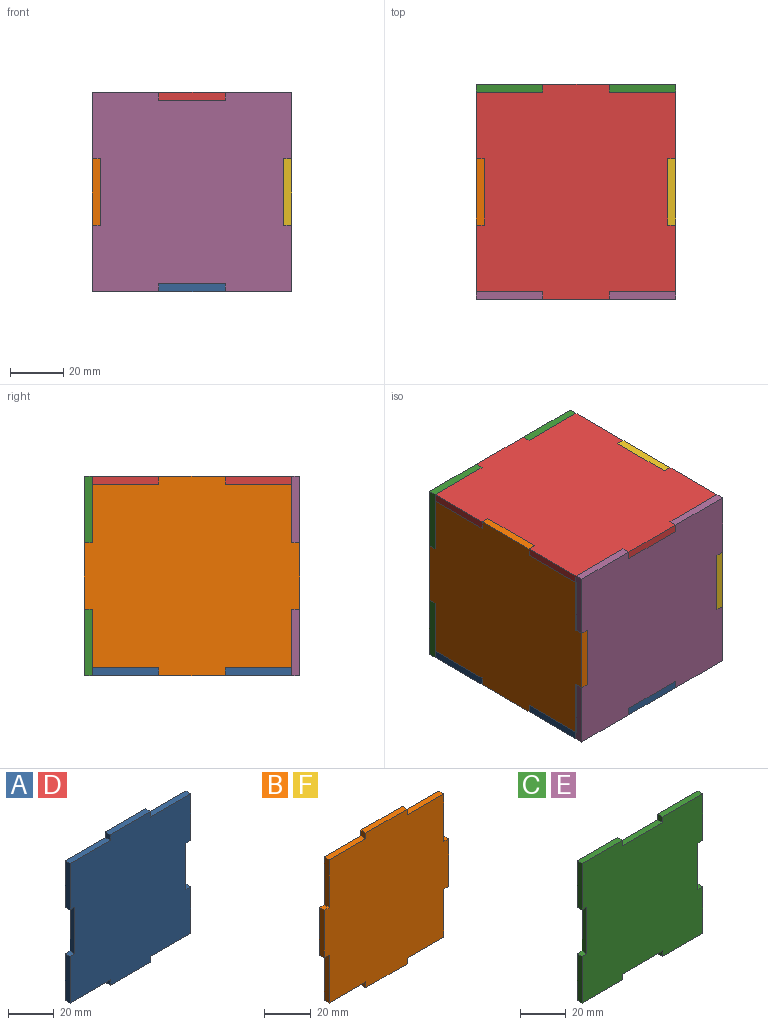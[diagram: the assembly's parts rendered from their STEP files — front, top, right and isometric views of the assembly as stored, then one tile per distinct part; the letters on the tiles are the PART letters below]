
ASSEMBLY  parts=6 mates=2
PART A: 22 faces, bbox 75x3x81 mm
  f0: plane 25x3mm, normal (0,0,1), area 75mm2, adj f1,f19,f20,f21
  f1: plane 3x3mm, normal (1,0,0), area 9mm2, adj f0,f2,f20,f21
  f2: plane 25x3mm, normal (0,0,1), area 75mm2, adj f1,f3,f20,f21
  f3: plane 3x3mm, normal (-1,0,0), area 9mm2, adj f2,f4,f20,f21
  f4: plane 25x3mm, normal (0,0,1), area 75mm2, adj f3,f5,f20,f21
  f5: plane 25x3mm, normal (-1,0,0), area 75mm2, adj f4,f6,f20,f21
  f6: plane 3x3mm, normal (0,0,-1), area 9mm2, adj f5,f7,f20,f21
  f7: plane 25x3mm, normal (-1,0,0), area 75mm2, adj f6,f8,f20,f21
  f8: plane 3x3mm, normal (0,0,1), area 9mm2, adj f7,f9,f20,f21
  f9: plane 25x3mm, normal (-1,0,0), area 75mm2, adj f8,f10,f20,f21
  f10: plane 25x3mm, normal (0,0,-1), area 75mm2, adj f9,f11,f20,f21
  f11: plane 3x3mm, normal (-1,0,0), area 9mm2, adj f10,f12,f20,f21
  f12: plane 25x3mm, normal (0,0,-1), area 75mm2, adj f11,f13,f20,f21
  f13: plane 3x3mm, normal (1,0,0), area 9mm2, adj f12,f14,f20,f21
  f14: plane 25x3mm, normal (0,0,-1), area 75mm2, adj f13,f15,f20,f21
  f15: plane 25x3mm, normal (1,0,0), area 75mm2, adj f14,f16,f20,f21
  f16: plane 3x3mm, normal (0,0,1), area 9mm2, adj f15,f17,f20,f21
  f17: plane 25x3mm, normal (1,0,0), area 75mm2, adj f16,f18,f20,f21
  f18: plane 3x3mm, normal (0,0,-1), area 9mm2, adj f17,f19,f20,f21
  f19: plane 25x3mm, normal (1,0,0), area 75mm2, adj f0,f18,f20,f21
  f20: plane 81x75mm, normal (0,-1,0), area 5625mm2, adj f0,f1,f2,f3,f4,f5,f6,f7
  f21: plane 81x75mm, normal (0,1,0), area 5625mm2, adj f0,f1,f2,f3,f4,f5,f6,f7
PART B: 22 faces, bbox 75x3x81 mm
  f0: plane 25x3mm, normal (0,0,1), area 75mm2, adj f1,f19,f20,f21
  f1: plane 3x3mm, normal (-1,0,0), area 9mm2, adj f0,f2,f20,f21
  f2: plane 22x3mm, normal (0,0,1), area 66mm2, adj f1,f3,f20,f21
  f3: plane 25x3mm, normal (-1,0,0), area 75mm2, adj f2,f4,f20,f21
  f4: plane 3x3mm, normal (0,0,1), area 9mm2, adj f3,f5,f20,f21
  f5: plane 25x3mm, normal (-1,0,0), area 75mm2, adj f4,f6,f20,f21
  f6: plane 3x3mm, normal (0,0,-1), area 9mm2, adj f5,f7,f20,f21
  f7: plane 25x3mm, normal (-1,0,0), area 75mm2, adj f6,f8,f20,f21
  f8: plane 22x3mm, normal (0,0,-1), area 66mm2, adj f7,f9,f20,f21
  f9: plane 3x3mm, normal (-1,0,0), area 9mm2, adj f8,f10,f20,f21
  f10: plane 25x3mm, normal (0,0,-1), area 75mm2, adj f9,f11,f20,f21
  f11: plane 3x3mm, normal (1,0,0), area 9mm2, adj f10,f12,f20,f21
  f12: plane 22x3mm, normal (0,0,-1), area 66mm2, adj f11,f13,f20,f21
  f13: plane 25x3mm, normal (1,0,0), area 75mm2, adj f12,f14,f20,f21
  f14: plane 3x3mm, normal (0,0,-1), area 9mm2, adj f13,f15,f20,f21
  f15: plane 25x3mm, normal (1,0,0), area 75mm2, adj f14,f16,f20,f21
  f16: plane 3x3mm, normal (0,0,1), area 9mm2, adj f15,f17,f20,f21
  f17: plane 25x3mm, normal (1,0,0), area 75mm2, adj f16,f18,f20,f21
  f18: plane 22x3mm, normal (0,0,1), area 66mm2, adj f17,f19,f20,f21
  f19: plane 3x3mm, normal (1,0,0), area 9mm2, adj f0,f18,f20,f21
  f20: plane 81x75mm, normal (0,-1,0), area 5475mm2, adj f0,f1,f2,f3,f4,f5,f6,f7
  f21: plane 81x75mm, normal (0,1,0), area 5475mm2, adj f0,f1,f2,f3,f4,f5,f6,f7
PART C: 22 faces, bbox 75x3x75 mm
  f0: plane 3x3mm, normal (1,0,0), area 9mm2, adj f1,f19,f20,f21
  f1: plane 25x3mm, normal (0,0,1), area 75mm2, adj f0,f2,f20,f21
  f2: plane 25x3mm, normal (-1,0,0), area 75mm2, adj f1,f3,f20,f21
  f3: plane 3x3mm, normal (0,0,-1), area 9mm2, adj f2,f4,f20,f21
  f4: plane 25x3mm, normal (-1,0,0), area 75mm2, adj f3,f5,f20,f21
  f5: plane 3x3mm, normal (0,0,1), area 9mm2, adj f4,f6,f20,f21
  f6: plane 25x3mm, normal (-1,0,0), area 75mm2, adj f5,f7,f20,f21
  f7: plane 25x3mm, normal (0,0,-1), area 75mm2, adj f6,f8,f20,f21
  f8: plane 3x3mm, normal (1,0,0), area 9mm2, adj f7,f9,f20,f21
  f9: plane 25x3mm, normal (0,0,-1), area 75mm2, adj f8,f10,f20,f21
  f10: plane 3x3mm, normal (-1,0,0), area 9mm2, adj f9,f11,f20,f21
  f11: plane 25x3mm, normal (0,0,-1), area 75mm2, adj f10,f12,f20,f21
  f12: plane 25x3mm, normal (1,0,0), area 75mm2, adj f11,f13,f20,f21
  f13: plane 3x3mm, normal (0,0,1), area 9mm2, adj f12,f14,f20,f21
  f14: plane 25x3mm, normal (1,0,0), area 75mm2, adj f13,f15,f20,f21
  f15: plane 3x3mm, normal (0,0,-1), area 9mm2, adj f14,f16,f20,f21
  f16: plane 25x3mm, normal (1,0,0), area 75mm2, adj f15,f17,f20,f21
  f17: plane 25x3mm, normal (0,0,1), area 75mm2, adj f16,f18,f20,f21
  f18: plane 3x3mm, normal (-1,0,0), area 9mm2, adj f17,f19,f20,f21
  f19: plane 25x3mm, normal (0,0,1), area 75mm2, adj f0,f18,f20,f21
  f20: plane 75x75mm, normal (0,-1,0), area 5325mm2, adj f0,f1,f2,f3,f4,f5,f6,f7
  f21: plane 75x75mm, normal (0,1,0), area 5325mm2, adj f0,f1,f2,f3,f4,f5,f6,f7
PART D: same geometry as A
PART E: same geometry as C
PART F: same geometry as B
PLACE A rot(axis=(-1,0,0),90deg) t=(-50.13,17.7,-21.54)mm
PLACE B rot(axis=(-0.58,-0.58,-0.58),120deg) t=(-84.63,17.7,19.25)mm
PLACE C t=(-50.13,58.2,15.96)mm
PLACE D rot(axis=(-1,0,0),90deg) t=(-50.13,17.7,50.46)mm
PLACE E t=(-50.13,-19.8,15.96)mm
PLACE F rot(axis=(-0.58,-0.58,-0.58),120deg) t=(-12.63,17.7,19.25)mm
MATE slider B.f19 <-> C.f3  axis (0,0,1) through (-87.63,58.2,28.46)mm
MATE slider A.f7 <-> B.f21  axis (-1,0,0) through (-84.63,17.7,-21.54)mm
